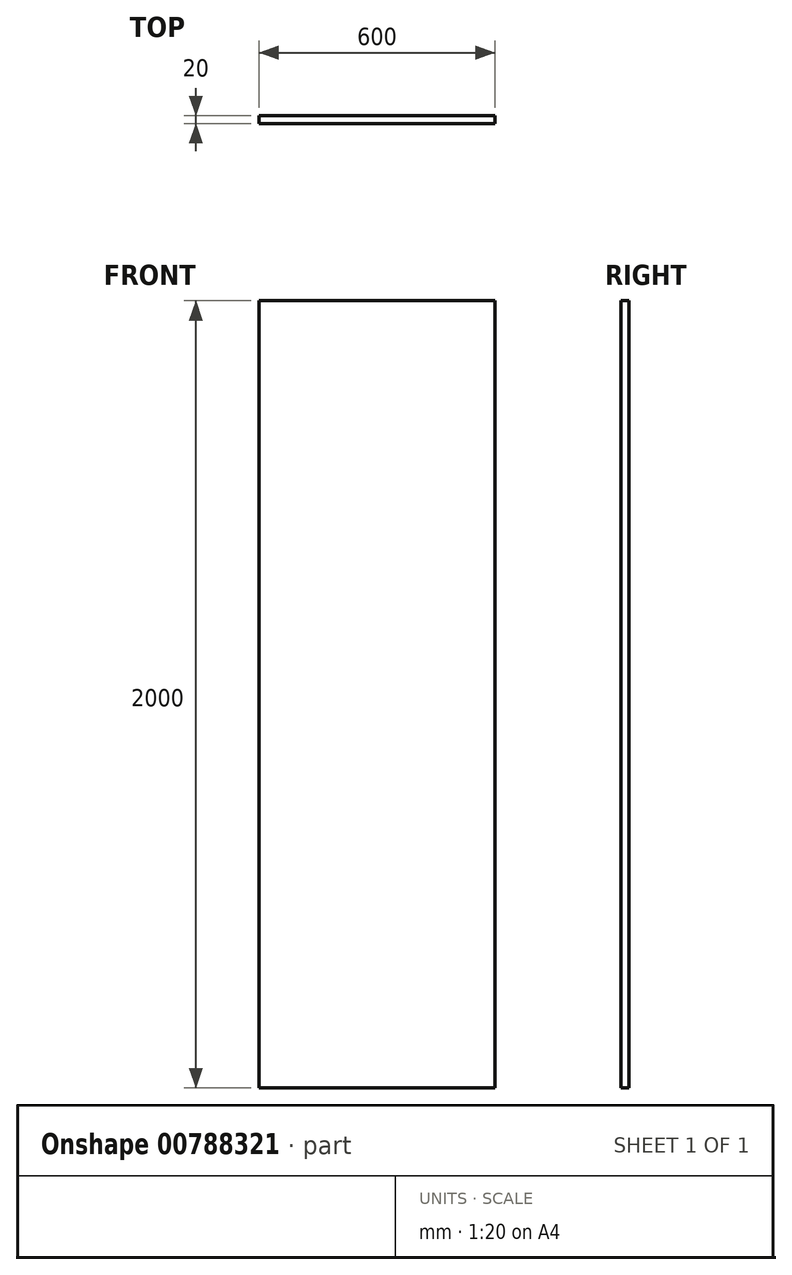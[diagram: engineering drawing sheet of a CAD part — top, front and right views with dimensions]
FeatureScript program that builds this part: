
annotation { "Feature Type Name" : "Feature", "Feature Type Description" : "" }
export const myFeature = defineFeature(function(context is Context, id is Id, definition is map)
    precondition{}
    {
        {
            var Q0;
            Q0=qCreatedBy(makeId("Front.planeOp"),FACE);
            var sketch = newSketch(context, id + "F0", { "sketchPlane" : qUnion([Q0])});
            skLineSegment(sketch, "E0.bottom", {"start": v(300, -1000) * mm, "end": v(-300, -1000) * mm});
            skLineSegment(sketch, "E0.top", {"start": v(300, 1000) * mm, "end": v(-300, 1000) * mm});
            skLineSegment(sketch, "E0.left", {"start": v(300, -1000) * mm, "end": v(300, 1000) * mm});
            skLineSegment(sketch, "E0.right", {"start": v(-300, -1000) * mm, "end": v(-300, 1000) * mm});
            skPoint(sketch, "E0.middle", {"position": v(0, 0) * mm});
            skLineSegment(sketch, "E1", {"start": v(0, 1000) * mm, "end": v(0, -1000) * mm});
            skLineSegment(sketch, "E2", {"start": v(0, -1000) * mm, "end": v(0, 745.48) * mm, "construction": true});
            skSolve(sketch);
        }
        {
            var Q0;
            Q0=makeQuery(id+"F0.imprint","IMPRINT",FACE,{"disambiguationData":[TD([[makeQuery(id+"F0.imprint","IMPRINT",EDGE,{"derivedFrom":sQuery(id+"F0.wireOp",EDGE,"E0.bottom")}),-1.0]])]});
            extrude(context, id + "F1", {"entities" : qUnion([Q0]), "depth" : 20 * mm, "offsetDistance" : 25 * mm});
        }
    });
